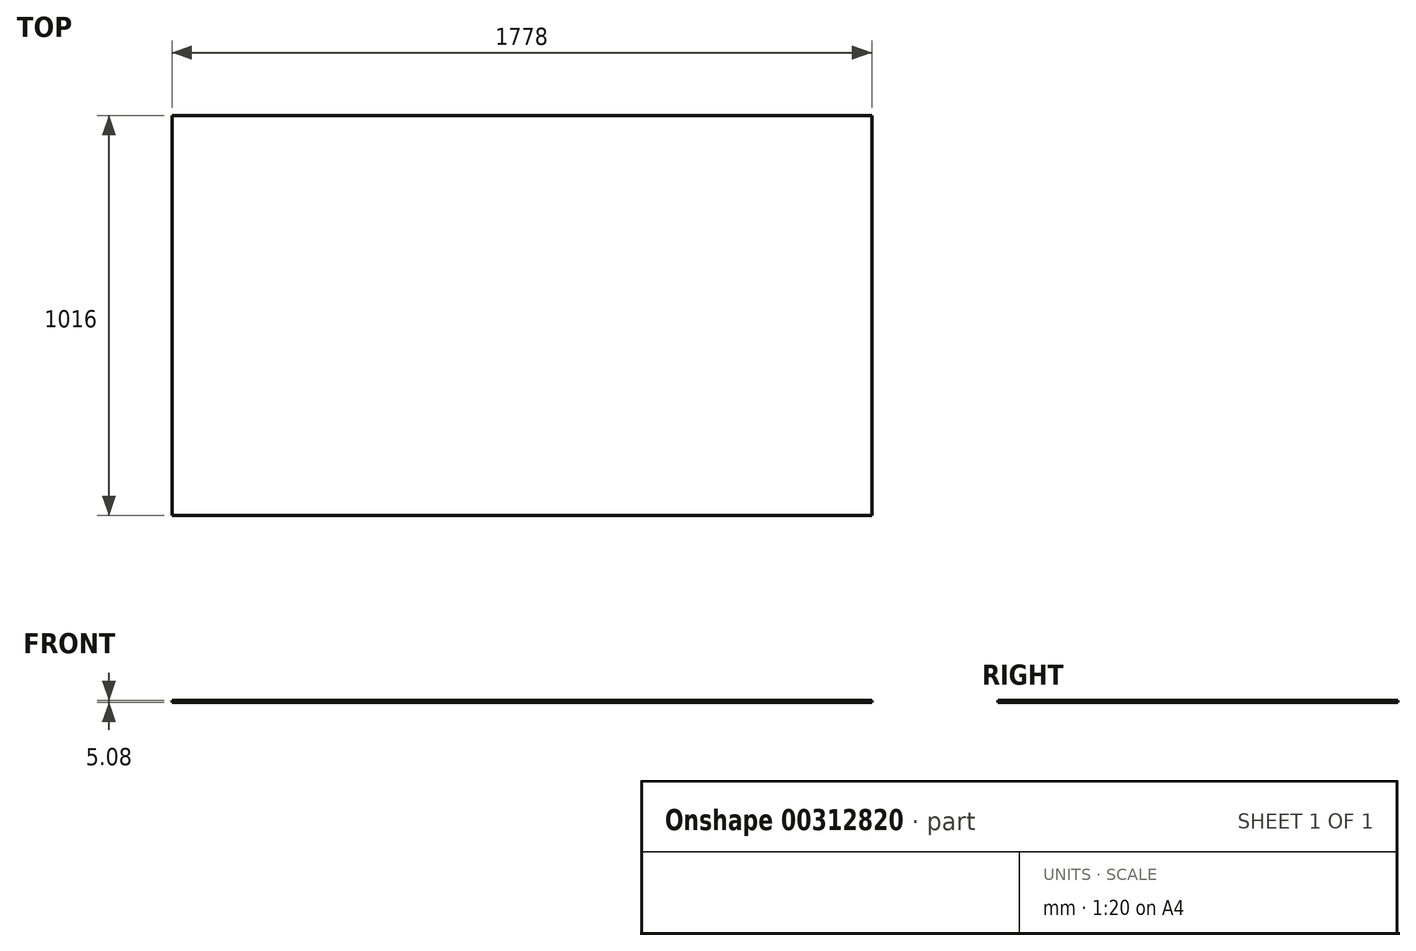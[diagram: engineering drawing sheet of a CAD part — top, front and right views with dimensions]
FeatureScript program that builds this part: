
annotation { "Feature Type Name" : "Feature", "Feature Type Description" : "" }
export const myFeature = defineFeature(function(context is Context, id is Id, definition is map)
    precondition{}
    {
        {
            var Q0;
            Q0=qCreatedBy(makeId("Top.planeOp"),FACE);
            var sketch = newSketch(context, id + "F0", { "sketchPlane" : qUnion([Q0])});
            skLineSegment(sketch, "E0.bottom", {"start": v(-921.8, 742.3) * mm, "end": v(856.2, 742.3) * mm});
            skLineSegment(sketch, "E0.top", {"start": v(-921.8, -273.7) * mm, "end": v(856.2, -273.7) * mm});
            skLineSegment(sketch, "E0.left", {"start": v(-921.8, 742.3) * mm, "end": v(-921.8, -273.7) * mm});
            skLineSegment(sketch, "E0.right", {"start": v(856.2, 742.3) * mm, "end": v(856.2, -273.7) * mm});
            skSolve(sketch);
        }
        {
            var Q0;
            Q0 = qSketchRegion(id + "F0", true);
            extrude(context, id + "F1", {"entities" : qUnion([Q0]), "depth" : 5.08 * mm});
        }
    });
